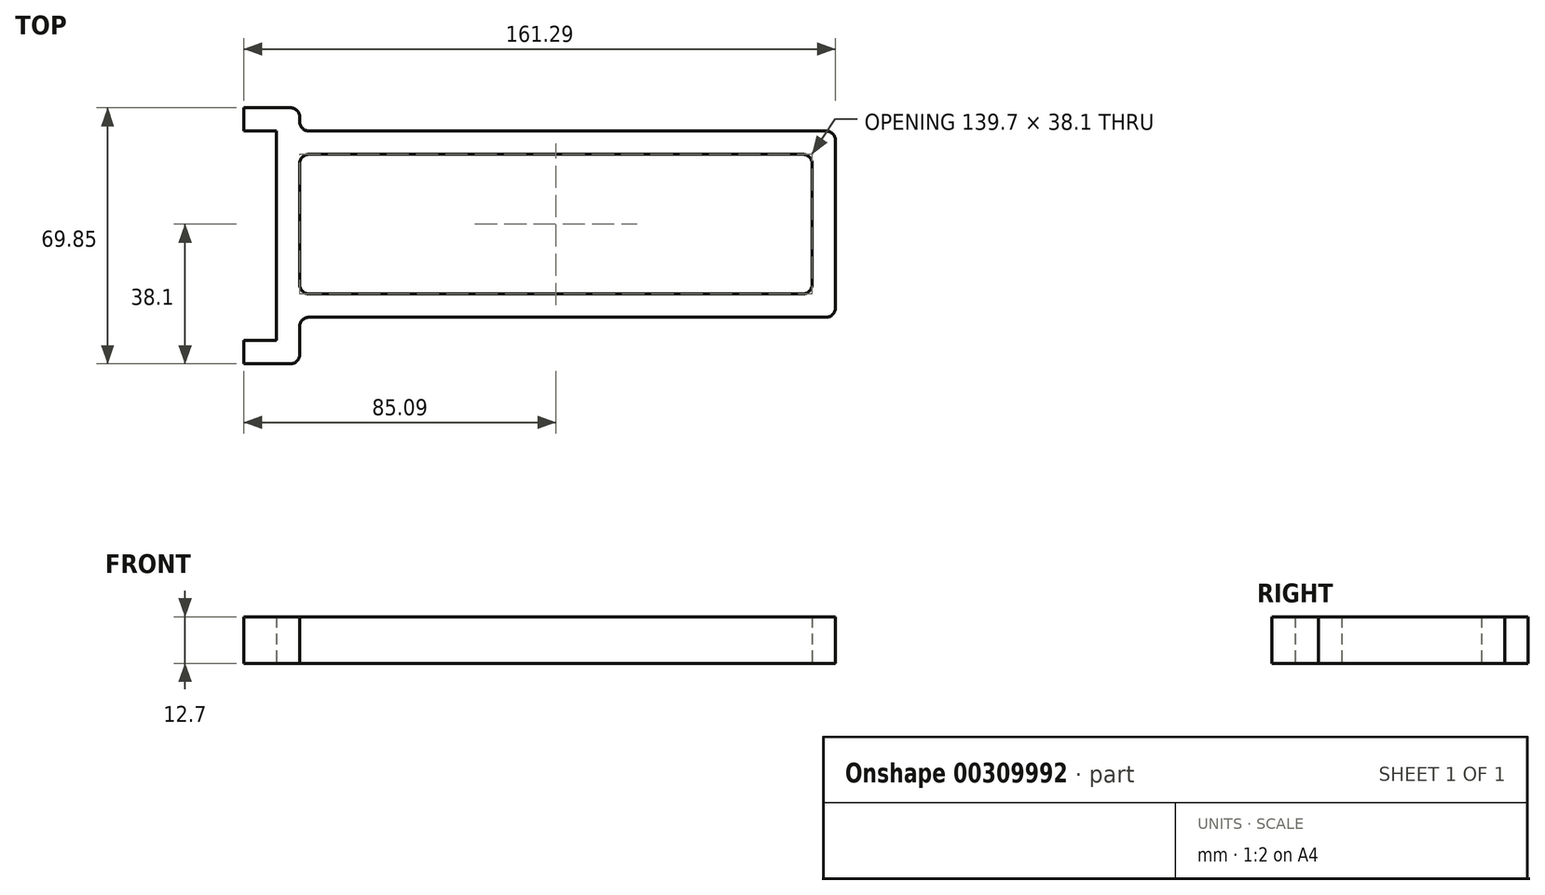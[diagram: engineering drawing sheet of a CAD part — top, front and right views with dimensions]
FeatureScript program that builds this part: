
annotation { "Feature Type Name" : "Feature", "Feature Type Description" : "" }
export const myFeature = defineFeature(function(context is Context, id is Id, definition is map)
    precondition{}
    {
        {
            var Q0;
            Q0=qCreatedBy(makeId("Top.planeOp"),FACE);
            var sketch = newSketch(context, id + "F0", { "sketchPlane" : qUnion([Q0])});
            skLineSegment(sketch, "E0.bottom", {"start": v(-69.85, 19.05) * mm, "end": v(69.85, 19.05) * mm});
            skLineSegment(sketch, "E0.top", {"start": v(-69.85, -19.05) * mm, "end": v(69.85, -19.05) * mm});
            skLineSegment(sketch, "E0.left", {"start": v(-69.85, 19.05) * mm, "end": v(-69.85, -19.05) * mm});
            skLineSegment(sketch, "E0.right", {"start": v(69.85, 19.05) * mm, "end": v(69.85, -19.05) * mm});
            skLineSegment(sketch, "E1", {"start": v(-69.85, 19.05) * mm, "end": v(69.85, -19.05) * mm, "construction": true});
            skLineSegment(sketch, "E2.0", {"start": v(76.2, 25.4) * mm, "end": v(76.2, -25.4) * mm});
            skLineSegment(sketch, "E2.1", {"start": v(-76.2, 25.4) * mm, "end": v(76.2, 25.4) * mm});
            skLineSegment(sketch, "E2.2", {"start": v(-76.2, 25.4) * mm, "end": v(-76.2, -25.4) * mm});
            skLineSegment(sketch, "E2.3", {"start": v(-76.2, -25.4) * mm, "end": v(76.2, -25.4) * mm});
            skSolve(sketch);
        }
        {
            var Q0;
            Q0 = qSketchRegion(id + "F0", true);
            extrude(context, id + "F1", {"entities" : qUnion([Q0]), "depth" : 12.7 * mm});
        }
        {
            var Q0;
            Q0=qCreatedBy(makeId("Top.planeOp"),FACE);
            var sketch = newSketch(context, id + "F2", { "sketchPlane" : qUnion([Q0])});
            skLineSegment(sketch, "E3", {"start": v(-69.85, 31.75) * mm, "end": v(-97.8, 31.75) * mm});
            skLineSegment(sketch, "E4", {"start": v(-97.8, 31.75) * mm, "end": v(-97.8, -38.1) * mm});
            skLineSegment(sketch, "E5", {"start": v(-97.8, -38.1) * mm, "end": v(-69.85, -38.1) * mm});
            skLineSegment(sketch, "E6", {"start": v(-69.85, 31.75) * mm, "end": v(-69.85, -38.1) * mm});
            skLineSegment(sketch, "E7.bottom", {"start": v(-85.1, 25.4) * mm, "end": v(-76.2, 25.4) * mm});
            skLineSegment(sketch, "E7.top", {"start": v(-85.1, -31.75) * mm, "end": v(-76.2, -31.75) * mm});
            skLineSegment(sketch, "E7.left", {"start": v(-85.1, 25.4) * mm, "end": v(-85.1, -31.75) * mm});
            skLineSegment(sketch, "E7.right", {"start": v(-76.2, 25.4) * mm, "end": v(-76.2, -31.75) * mm});
            skSolve(sketch);
        }
        {
            var Q0;
            Q0 = qSketchRegion(id + "F2", true);
            extrude(context, id + "F3", {"entities" : qUnion([Q0]), "operationType" : NewBodyOperationType.ADD, "depth" : 12.7 * mm});
        }
        {
            var Q0;
            Q0=makeQuery(id+"F1.opExtrude","SWEPT_EDGE",EDGE,{"disambiguationData":[OSD([sQuery(id+"F0.wireOp",EDGE,"E0.bottom"),sQuery(id+"F0.wireOp",EDGE,"E0.left")])]});
            var Q1;
            Q1=makeQuery(id+"F1.opExtrude","SWEPT_EDGE",EDGE,{"disambiguationData":[OSD([sQuery(id+"F0.wireOp",EDGE,"E0.bottom"),sQuery(id+"F0.wireOp",EDGE,"E0.right")])]});
            var Q2;
            Q2=makeQuery(id+"F1.opExtrude","SWEPT_EDGE",EDGE,{"disambiguationData":[OSD([sQuery(id+"F0.wireOp",EDGE,"E0.top"),sQuery(id+"F0.wireOp",EDGE,"E0.right")])]});
            var Q3;
            Q3=makeQuery(id+"F1.opExtrude","SWEPT_EDGE",EDGE,{"disambiguationData":[OSD([sQuery(id+"F0.wireOp",EDGE,"E0.top"),sQuery(id+"F0.wireOp",EDGE,"E0.left")])]});
            var Q4;
            Q4=makeQuery(id+"F3.boolean.opBoolean","INTERSECT",EDGE,{"derivedFrom":[makeQuery(id+"F1.opExtrude","SWEPT_FACE",FACE,{"disambiguationData":[OSD([sQuery(id+"F0.wireOp",EDGE,"E2.1")])]}),makeQuery(id+"F3.opExtrude","SWEPT_FACE",FACE,{"disambiguationData":[OSD([sQuery(id+"F2.wireOp",EDGE,"E6")])]})]});
            var Q5;
            Q5=makeQuery(id+"F1.opExtrude","SWEPT_EDGE",EDGE,{"disambiguationData":[OSD([sQuery(id+"F0.wireOp",EDGE,"E2.0"),sQuery(id+"F0.wireOp",EDGE,"E2.1")])]});
            var Q6;
            Q6=makeQuery(id+"F1.opExtrude","SWEPT_EDGE",EDGE,{"disambiguationData":[OSD([sQuery(id+"F0.wireOp",EDGE,"E2.0"),sQuery(id+"F0.wireOp",EDGE,"E2.3")])]});
            var Q7;
            Q7=makeQuery(id+"F3.boolean.opBoolean","INTERSECT",EDGE,{"derivedFrom":[makeQuery(id+"F1.opExtrude","SWEPT_FACE",FACE,{"disambiguationData":[OSD([sQuery(id+"F0.wireOp",EDGE,"E2.3")])]}),makeQuery(id+"F3.opExtrude","SWEPT_FACE",FACE,{"disambiguationData":[OSD([sQuery(id+"F2.wireOp",EDGE,"E6")])]})]});
            var Q8;
            Q8=makeQuery(id+"F3.opExtrude","SWEPT_EDGE",EDGE,{"disambiguationData":[OSD([sQuery(id+"F2.wireOp",EDGE,"E3"),sQuery(id+"F2.wireOp",EDGE,"E6")])]});
            var Q9;
            Q9=makeQuery(id+"F3.opExtrude","SWEPT_EDGE",EDGE,{"disambiguationData":[OSD([sQuery(id+"F2.wireOp",EDGE,"E5"),sQuery(id+"F2.wireOp",EDGE,"E6")])]});
            fillet(context, id + "F4", {"entities" : qUnion([Q0, Q1, Q2, Q3, Q4, Q5, Q6, Q7, Q8, Q9]), "radius" : 2.54 * mm, "tangentPropagation" : true, "allowEdgeOverflow" : false});
        }
        {
            var Q0;
            Q0=makeQuery(id+"F3.boolean.opBoolean","MERGE",FACE,{"derivedFrom":[makeQuery(id+"F1.opExtrude","CAP_FACE",FACE,{"disambiguationData":[OSD([sQuery(id+"F0.wireOp",EDGE,"E0.bottom"),sQuery(id+"F0.wireOp",EDGE,"E0.top"),sQuery(id+"F0.wireOp",EDGE,"E0.left"),sQuery(id+"F0.wireOp",EDGE,"E0.right"),sQuery(id+"F0.wireOp",EDGE,"E2.0"),sQuery(id+"F0.wireOp",EDGE,"E2.1"),sQuery(id+"F0.wireOp",EDGE,"E2.2"),sQuery(id+"F0.wireOp",EDGE,"E2.3")])],"isStart":true}),makeQuery(id+"F3.opExtrude","CAP_FACE",FACE,{"disambiguationData":[OSD([sQuery(id+"F2.wireOp",EDGE,"E3"),sQuery(id+"F2.wireOp",EDGE,"E4"),sQuery(id+"F2.wireOp",EDGE,"E5"),sQuery(id+"F2.wireOp",EDGE,"E6"),sQuery(id+"F2.wireOp",EDGE,"E7.bottom"),sQuery(id+"F2.wireOp",EDGE,"E7.top"),sQuery(id+"F2.wireOp",EDGE,"E7.left"),sQuery(id+"F2.wireOp",EDGE,"E7.right")])],"isStart":true})]});
            var sketch = newSketch(context, id + "F5", { "sketchPlane" : qUnion([Q0])});
            skLineSegment(sketch, "E8.bottom", {"start": v(-85.1, -31.75) * mm, "end": v(-97.8, -31.75) * mm});
            skLineSegment(sketch, "E8.top", {"start": v(-85.1, 38.1) * mm, "end": v(-97.8, 38.1) * mm});
            skLineSegment(sketch, "E8.left", {"start": v(-85.1, -31.75) * mm, "end": v(-85.1, 38.1) * mm});
            skLineSegment(sketch, "E8.right", {"start": v(-97.8, -31.75) * mm, "end": v(-97.8, 38.1) * mm});
            skSolve(sketch);
        }
        {
            var Q0;
            {var subQ3=sQuery(id+"F5.wireOp",EDGE,"E8.bottom");Q0=makeQuery(id+"F5.imprint","IMPRINT",FACE,{"disambiguationData":[TD([[makeQuery(id+"F5.imprint","IMPRINT",EDGE,{"derivedFrom":subQ3}),-1.0]])]});}
            extrude(context, id + "F6", {"entities" : qUnion([Q0]), "operationType" : NewBodyOperationType.REMOVE, "endBound" : BoundingType.THROUGH_ALL, "oppositeDirection" : true, "depth" : 25.4 * mm});
        }
    });
